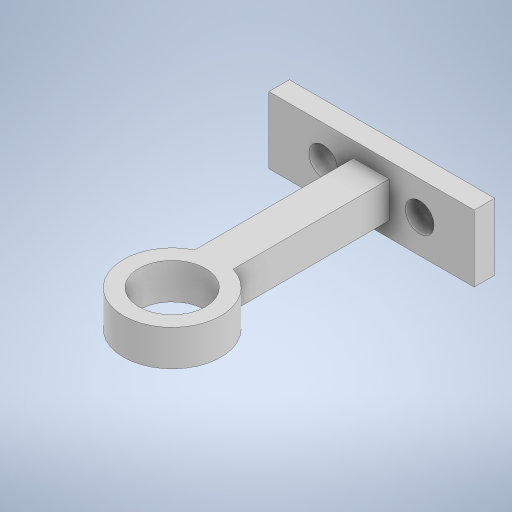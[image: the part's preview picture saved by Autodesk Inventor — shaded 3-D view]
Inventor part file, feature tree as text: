
AUTODESK INVENTOR PART (.ipt)
format: ipt  version: 2023 (Build 270158000, 158)  size: 262,144 bytes
history: native  units: mm
features: extrude x3, sketch x3, other x1, plane x1
ambient origin geometry x8: Origin, YZ Plane, XZ Plane, XY Plane, X Axis, Y Axis, Z Axis, Center Point
bodies: Body1 (feature_tree)
feature tree (8):
  other  "實體1"
  extrude  "擠出1"  Depth=40.0mm
  extrude  "擠出2"  Depth=13.0mm
  plane  "工作平面2"
  extrude  "擠出3"  Depth=5.6mm
  sketch  "草圖1"
  sketch  "草圖3"
  sketch  "草圖4"
